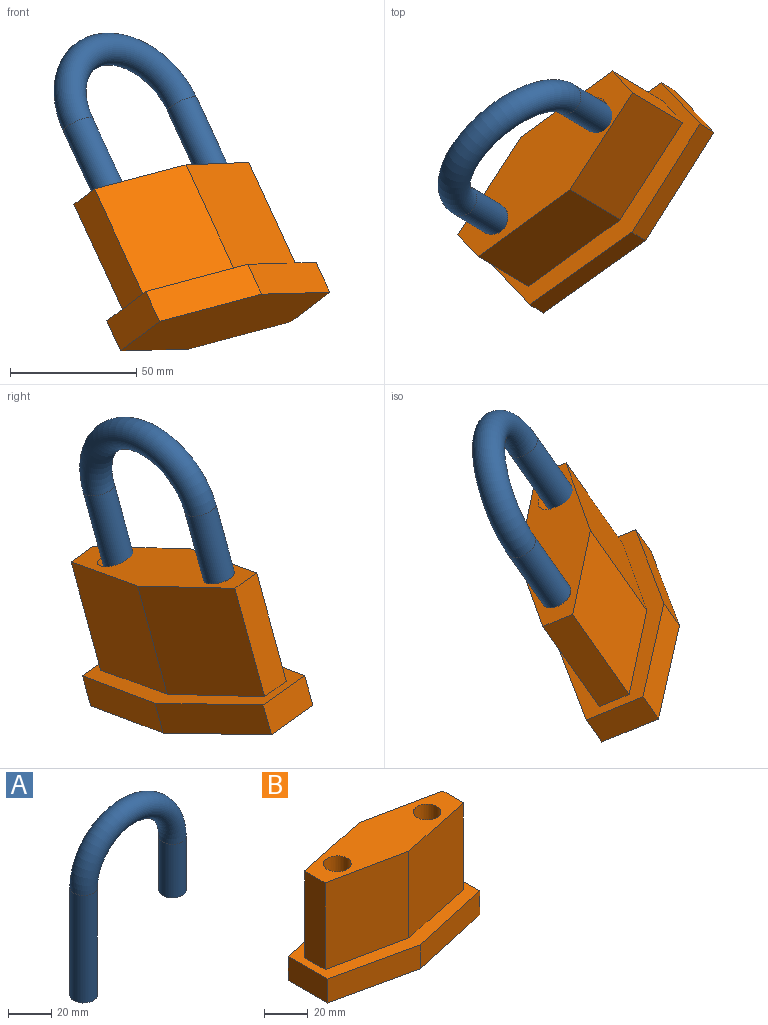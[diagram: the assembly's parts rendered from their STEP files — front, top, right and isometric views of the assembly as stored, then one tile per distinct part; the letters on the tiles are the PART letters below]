
ASSEMBLY  parts=2 mates=1
PART A: 5 faces, bbox 76.8x12.7x99.4 mm
  f0: plane 12.7x12.7mm, normal (0,0,-1), area 126.7mm2, adj f2
  f1: plane 12.7x12.7mm, normal (0,0,-1), area 126.7mm2, adj f4
  f2: cylinder r=6.35mm len=30.48mm, axis (0,0,1), area 1216.1mm2, adj f0,f3
  f3: torus R=29.13mm, axis (0,-1,0), area 3651.6mm2, adj f2,f4
  f4: cylinder r=6.35mm len=60.96mm, axis (0,0,-1), area 2432.2mm2, adj f1,f3
PART B: 19 faces, bbox 99.2x47.4x62.2 mm
  f0: plane 49.6x13.46mm, normal (0.22,0.98,0), area 683.9mm2, adj f1,f5,f6,f7
  f1: plane 49.6x13.46mm, normal (-0.22,0.98,0), area 683.9mm2, adj f0,f2,f6,f7
  f2: plane 25.4x13.46mm, normal (-1,0,0), area 341.9mm2, adj f1,f3,f6,f7
  f3: plane 49.6x13.46mm, normal (-0.22,-0.98,0), area 683.9mm2, adj f2,f4,f6,f7
  f4: plane 49.6x13.46mm, normal (0.22,-0.98,0), area 683.9mm2, adj f3,f5,f6,f7
  f5: plane 25.4x13.46mm, normal (1,0,0), area 341.9mm2, adj f0,f4,f6,f7
  f6: plane 99.19x47.39mm, normal (0,0,1), area 1565.7mm2, adj f0,f1,f2,f3,f4,f5,f8,f9
  f7: plane 99.19x47.39mm, normal (0,0,-1), area 3610.1mm2, adj f0,f1,f2,f3,f4,f5
  f8: plane 48.77x44.93mm, normal (0.2,0.98,0), area 2238.6mm2, adj f6,f9,f13,f14
  f9: plane 48.77x44.93mm, normal (-0.2,0.98,0), area 2238.6mm2, adj f6,f8,f10,f14
  f10: plane 48.77x13.35mm, normal (-1,0,0), area 651.1mm2, adj f6,f9,f11,f14
  f11: plane 48.77x44.93mm, normal (-0.2,-0.98,0), area 2238.6mm2, adj f6,f10,f12,f14
  f12: plane 48.77x44.93mm, normal (0.2,-0.98,0), area 2238.6mm2, adj f6,f11,f13,f14
  f13: plane 48.77x13.35mm, normal (1,0,0), area 651.1mm2, adj f6,f8,f12,f14
  f14: plane 89.86x32.15mm, normal (0,0,1), area 1791mm2, adj f8,f9,f10,f11,f12,f13,f15,f17
  f15: cylinder r=6.35mm len=30.48mm, axis (0,0,1), area 1216.1mm2, adj f14,f16
  f16: plane 12.7x12.7mm, normal (0,0,1), area 126.7mm2, adj f15
  f17: cylinder r=6.35mm len=30.48mm, axis (0,0,1), area 1216.1mm2, adj f14,f18
  f18: plane 12.7x12.7mm, normal (0,0,1), area 126.7mm2, adj f17
PLACE A rot(axis=(0.16,-0.21,-0.97),138.9deg) t=(-177.16,-70.28,-45.86)mm
PLACE B rot(axis=(-0.44,-0.33,0.84),52.8deg) t=(-113.58,-22.46,-29.58)mm
MATE revolute A.f2 <-> B.f17  axis (0.41,-0.24,-0.88) through (-170.27,-32.06,17.5)mm
